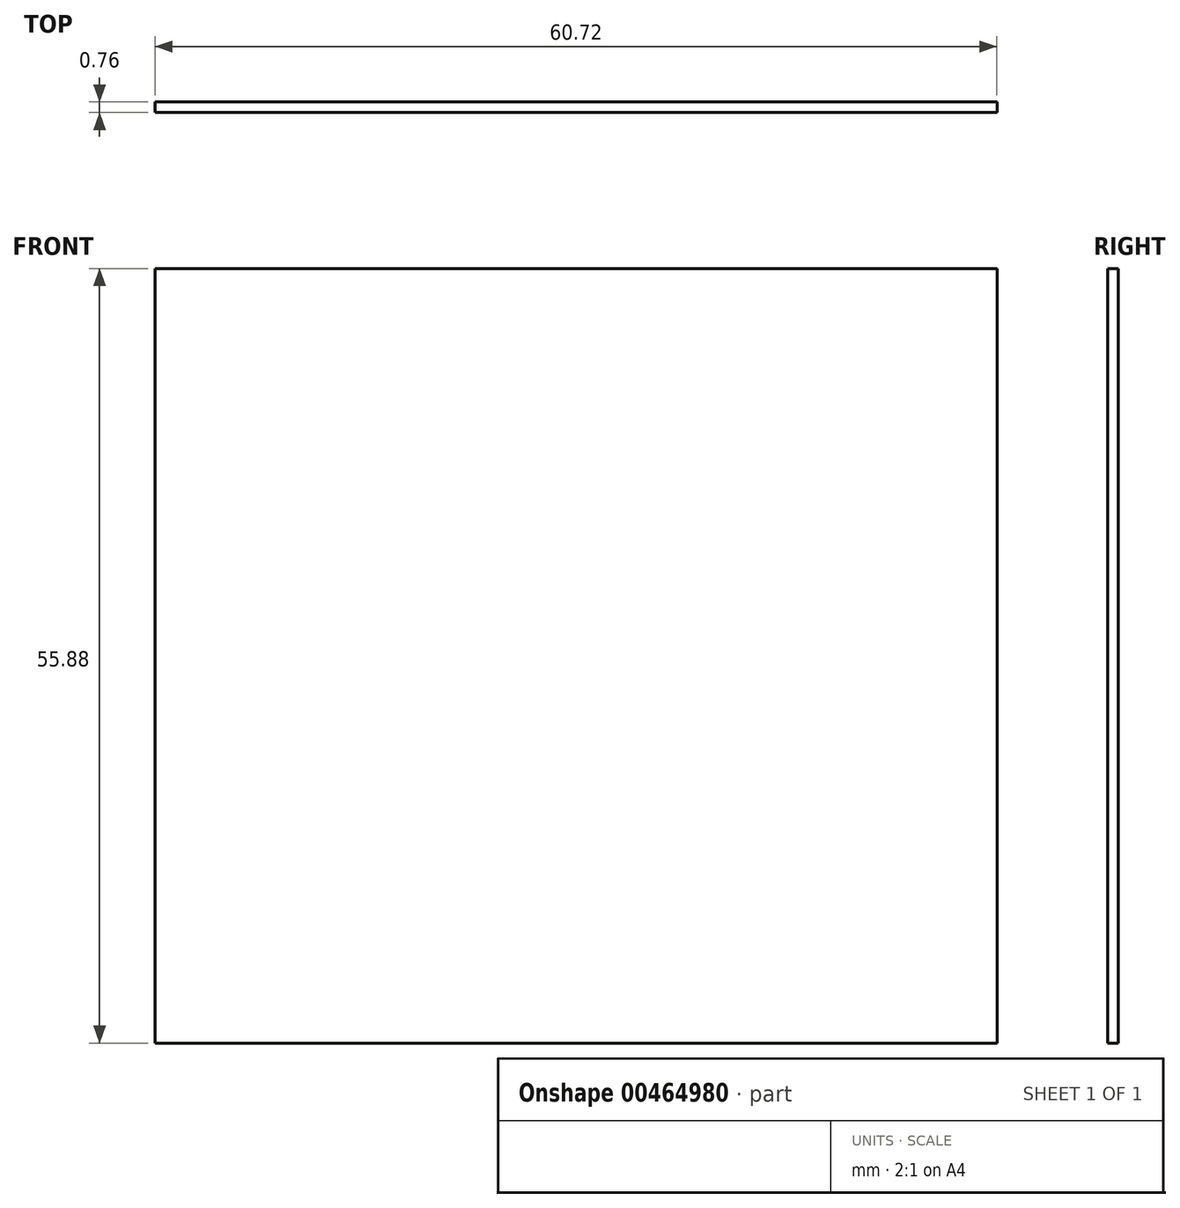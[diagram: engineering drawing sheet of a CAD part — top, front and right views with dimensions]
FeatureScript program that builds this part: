
annotation { "Feature Type Name" : "Feature", "Feature Type Description" : "" }
export const myFeature = defineFeature(function(context is Context, id is Id, definition is map)
    precondition{}
    {
        {
            var Q0;
            Q0=qCreatedBy(makeId("Front.planeOp"),FACE);
            var sketch = newSketch(context, id + "F0", { "sketchPlane" : qUnion([Q0])});
            skLineSegment(sketch, "E0.bottom", {"start": v(-30.36, 22.5) * mm, "end": v(30.36, 22.5) * mm});
            skLineSegment(sketch, "E0.top", {"start": v(-30.36, -33.37) * mm, "end": v(30.36, -33.37) * mm});
            skLineSegment(sketch, "E0.left", {"start": v(-30.36, 22.5) * mm, "end": v(-30.36, -33.37) * mm});
            skLineSegment(sketch, "E0.right", {"start": v(30.36, 22.5) * mm, "end": v(30.36, -33.37) * mm});
            skSolve(sketch);
        }
        {
            var Q0;
            Q0=makeQuery(id+"F0.imprint","IMPRINT",FACE,{"disambiguationData":[TD([[makeQuery(id+"F0.imprint","IMPRINT",EDGE,{"derivedFrom":sQuery(id+"F0.wireOp",EDGE,"E0.bottom")}),-1.0]])]});
            extrude(context, id + "F1", {"entities" : qUnion([Q0]), "depth" : 0.76 * mm});
        }
    });
